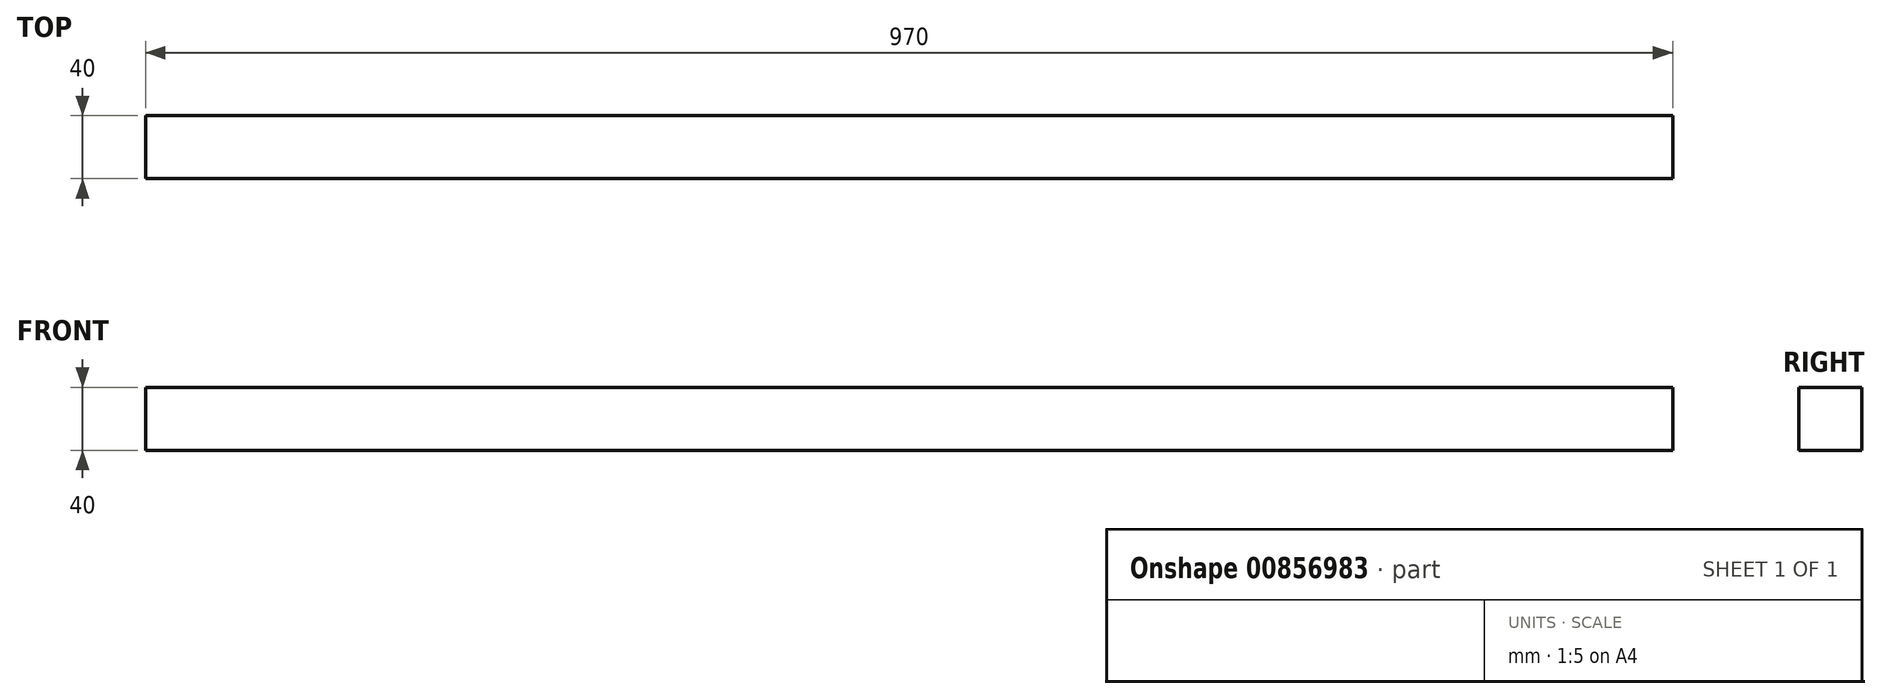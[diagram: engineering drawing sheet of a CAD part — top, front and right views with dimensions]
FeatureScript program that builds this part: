
annotation { "Feature Type Name" : "Feature", "Feature Type Description" : "" }
export const myFeature = defineFeature(function(context is Context, id is Id, definition is map)
    precondition{}
    {
        {
            var Q0;
            Q0=qCreatedBy(makeId("Right.planeOp"),FACE);
            var sketch = newSketch(context, id + "F0", { "sketchPlane" : qUnion([Q0])});
            skLineSegment(sketch, "E0.bottom", {"start": v(0, 0) * mm, "end": v(40, 0) * mm});
            skLineSegment(sketch, "E0.top", {"start": v(0, -40) * mm, "end": v(40, -40) * mm});
            skLineSegment(sketch, "E0.left", {"start": v(0, 0) * mm, "end": v(0, -40) * mm});
            skLineSegment(sketch, "E0.right", {"start": v(40, 0) * mm, "end": v(40, -40) * mm});
            skSolve(sketch);
        }
        {
            var Q0;
            Q0=makeQuery(id+"F0.imprint","IMPRINT",FACE,{"disambiguationData":[TD([[makeQuery(id+"F0.imprint","IMPRINT",EDGE,{"derivedFrom":sQuery(id+"F0.wireOp",EDGE,"E0.bottom")}),-1.0]])]});
            extrude(context, id + "F1", {"entities" : qUnion([Q0]), "depth" : 970 * mm, "offsetDistance" : 25 * mm});
        }
    });
